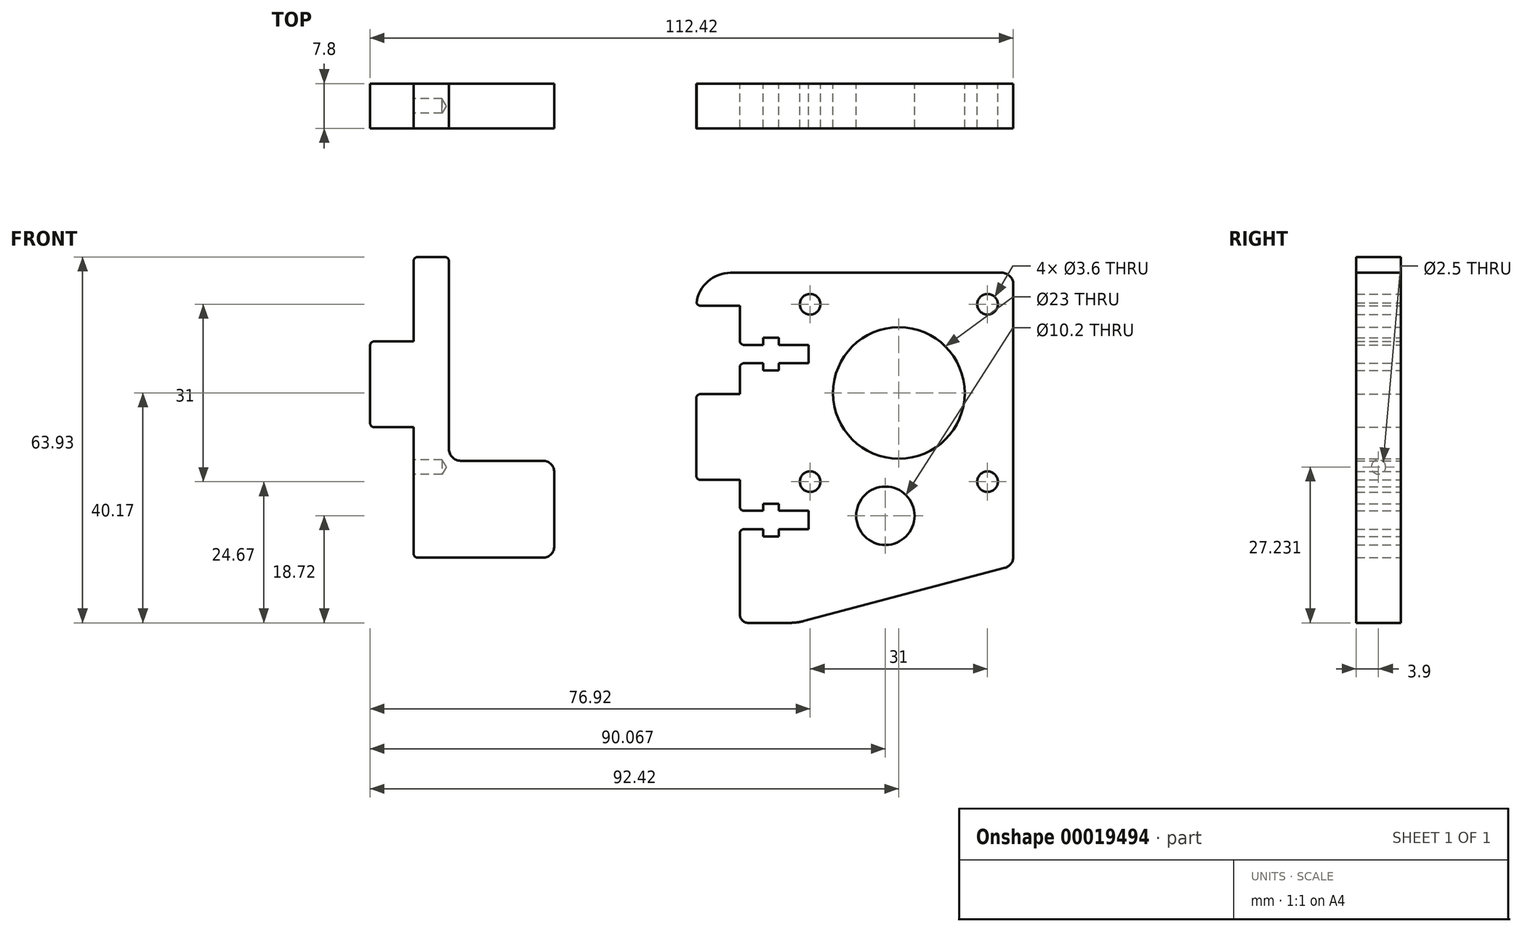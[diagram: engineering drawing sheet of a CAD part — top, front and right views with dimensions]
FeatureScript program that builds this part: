
annotation { "Feature Type Name" : "Feature", "Feature Type Description" : "" }
export const myFeature = defineFeature(function(context is Context, id is Id, definition is map)
    precondition{}
    {
        {
            var Q0;
            Q0=qCreatedBy(makeId("Front.planeOp"),FACE);
            var sketch = newSketch(context, id + "F0", { "sketchPlane" : qUnion([Q0])});
            skLineSegment(sketch, "E0.top", {"start": v(0.75, -5.75) * mm, "end": v(7.6, -5.75) * mm});
            skLineSegment(sketch, "E0.left", {"start": v(0, -5) * mm, "end": v(0, -6) * mm});
            skLineSegment(sketch, "E1", {"start": v(7.6, -21.2) * mm, "end": v(0.75, -21.2) * mm});
            skLineSegment(sketch, "E2", {"start": v(0, -21.95) * mm, "end": v(0, -35.45) * mm});
            skLineSegment(sketch, "E3", {"start": v(0.75, -36.2) * mm, "end": v(7.6, -36.2) * mm});
            skLineSegment(sketch, "E4", {"start": v(7.6, -36.2) * mm, "end": v(7.6, -40.85) * mm});
            skLineSegment(sketch, "E5", {"start": v(7.6, -21.2) * mm, "end": v(7.6, -16.55) * mm});
            skLineSegment(sketch, "E6", {"start": v(8.35, -15.8) * mm, "end": v(11.7, -15.8) * mm});
            skLineSegment(sketch, "E7", {"start": v(11.7, -15.8) * mm, "end": v(11.7, -17.05) * mm});
            skLineSegment(sketch, "E8", {"start": v(11.7, -17.05) * mm, "end": v(14.4, -17.05) * mm});
            skLineSegment(sketch, "E9", {"start": v(14.4, -17.05) * mm, "end": v(14.4, -15.8) * mm});
            skLineSegment(sketch, "E10", {"start": v(14.4, -15.8) * mm, "end": v(19.6, -15.8) * mm});
            skLineSegment(sketch, "E11", {"start": v(19.6, -15.8) * mm, "end": v(19.6, -12.6) * mm});
            skLineSegment(sketch, "E12", {"start": v(19.6, -12.6) * mm, "end": v(14.4, -12.6) * mm});
            skLineSegment(sketch, "E13", {"start": v(14.4, -12.6) * mm, "end": v(14.4, -11.35) * mm});
            skLineSegment(sketch, "E14", {"start": v(14.4, -11.35) * mm, "end": v(11.7, -11.35) * mm});
            skLineSegment(sketch, "E15", {"start": v(11.7, -11.35) * mm, "end": v(11.7, -12.6) * mm});
            skLineSegment(sketch, "E16", {"start": v(11.7, -12.6) * mm, "end": v(8.35, -12.6) * mm});
            skLineSegment(sketch, "E17", {"start": v(7.6, -11.85) * mm, "end": v(7.6, -5.75) * mm});
            skLineSegment(sketch, "E18", {"start": v(8.35, -41.6) * mm, "end": v(11.7, -41.6) * mm});
            skLineSegment(sketch, "E19", {"start": v(11.7, -41.6) * mm, "end": v(11.7, -40.35) * mm});
            skLineSegment(sketch, "E20", {"start": v(11.7, -40.35) * mm, "end": v(14.4, -40.35) * mm});
            skLineSegment(sketch, "E21", {"start": v(14.4, -40.35) * mm, "end": v(14.4, -41.6) * mm});
            skLineSegment(sketch, "E22", {"start": v(14.4, -41.6) * mm, "end": v(19.6, -41.6) * mm});
            skLineSegment(sketch, "E23", {"start": v(19.6, -41.6) * mm, "end": v(19.6, -44.8) * mm});
            skLineSegment(sketch, "E24", {"start": v(19.6, -44.8) * mm, "end": v(14.4, -44.8) * mm});
            skLineSegment(sketch, "E25", {"start": v(14.4, -44.8) * mm, "end": v(14.4, -46.05) * mm});
            skLineSegment(sketch, "E26", {"start": v(14.4, -46.05) * mm, "end": v(11.7, -46.05) * mm});
            skLineSegment(sketch, "E27", {"start": v(11.7, -46.05) * mm, "end": v(11.7, -44.8) * mm});
            skLineSegment(sketch, "E28", {"start": v(11.7, -44.8) * mm, "end": v(8.35, -44.8) * mm});
            skCircle(sketch, "E29", {"center": v(50.9, -5.5) * mm, "radius": 1.8 * mm});
            skCircle(sketch, "E30", {"center": v(50.9, -36.5) * mm, "radius": 1.8 * mm});
            skCircle(sketch, "E31.1.0.0", {"center": v(19.9, -5.5) * mm, "radius": 1.8 * mm});
            skCircle(sketch, "E31.1.0.1", {"center": v(19.9, -36.5) * mm, "radius": 1.8 * mm});
            skLineSegment(sketch, "E31.direction1", {"start": v(50.9, -5.5) * mm, "end": v(19.9, -5.5) * mm, "construction": true});
            skPoint(sketch, "E32.visualSharp", {"position": v(0, -5.75) * mm});
            skArc(sketch, "E32.filletArc", {"start": v(0, -5) * mm, "mid": v(0.22, -5.53) * mm, "end": v(0.75, -5.75) * mm});
            skPoint(sketch, "E33.visualSharp", {"position": v(0, -21.2) * mm});
            skArc(sketch, "E33.filletArc", {"start": v(0.75, -21.2) * mm, "mid": v(0.22, -21.42) * mm, "end": v(0, -21.95) * mm});
            skPoint(sketch, "E34.visualSharp", {"position": v(0, -36.2) * mm});
            skArc(sketch, "E34.filletArc", {"start": v(0, -35.45) * mm, "mid": v(0.22, -35.98) * mm, "end": v(0.75, -36.2) * mm});
            skLineSegment(sketch, "E35.trimOffspring", {"start": v(7.6, -45.55) * mm, "end": v(7.6, -59.67) * mm});
            skCircle(sketch, "E36", {"center": v(35.4, -21) * mm, "radius": 11.5 * mm});
            skCircle(sketch, "E37", {"center": v(33.05, -42.45) * mm, "radius": 5.1 * mm});
            skLineSegment(sketch, "E38", {"start": v(55.4, -2) * mm, "end": v(55.4, -49.63) * mm});
            skLineSegment(sketch, "E39", {"start": v(9.1, -61.17) * mm, "end": v(16.3, -61.17) * mm});
            skLineSegment(sketch, "E40", {"start": v(18.86, -60.84) * mm, "end": v(53.91, -51.56) * mm});
            skPoint(sketch, "E41.visualSharp", {"position": v(55.4, -51.17) * mm});
            skArc(sketch, "E41.filletArc", {"start": v(53.91, -51.56) * mm, "mid": v(54.98, -50.85) * mm, "end": v(55.4, -49.63) * mm});
            skPoint(sketch, "E42.visualSharp", {"position": v(7.6, -61.17) * mm});
            skArc(sketch, "E42.filletArc", {"start": v(7.6, -59.67) * mm, "mid": v(8.04, -60.73) * mm, "end": v(9.1, -61.17) * mm});
            skPoint(sketch, "E43.visualSharp", {"position": v(17.6, -61.17) * mm});
            skArc(sketch, "E43.filletArc", {"start": v(16.3, -61.17) * mm, "mid": v(17.59, -61.09) * mm, "end": v(18.86, -60.84) * mm});
            skPoint(sketch, "E44.visualSharp", {"position": v(7.6, -44.8) * mm});
            skArc(sketch, "E44.filletArc", {"start": v(8.35, -44.8) * mm, "mid": v(7.82, -45.02) * mm, "end": v(7.6, -45.55) * mm});
            skPoint(sketch, "E45.visualSharp", {"position": v(7.6, -41.6) * mm});
            skArc(sketch, "E45.filletArc", {"start": v(7.6, -40.85) * mm, "mid": v(7.82, -41.38) * mm, "end": v(8.35, -41.6) * mm});
            skPoint(sketch, "E46.visualSharp", {"position": v(7.6, -15.8) * mm});
            skArc(sketch, "E46.filletArc", {"start": v(8.35, -15.8) * mm, "mid": v(7.82, -16.02) * mm, "end": v(7.6, -16.55) * mm});
            skPoint(sketch, "E47.visualSharp", {"position": v(7.6, -12.6) * mm});
            skArc(sketch, "E47.filletArc", {"start": v(7.6, -11.85) * mm, "mid": v(7.82, -12.38) * mm, "end": v(8.35, -12.6) * mm});
            skLineSegment(sketch, "E48.trimOffspring", {"start": v(6, 0) * mm, "end": v(53.4, 0) * mm});
            skArc(sketch, "E49.filletArc", {"start": v(55.4, -2) * mm, "mid": v(54.81, -0.59) * mm, "end": v(53.4, 0) * mm});
            skPoint(sketch, "E50.orphan", {"position": v(0, 0) * mm});
            skArc(sketch, "E51.filletArc", {"start": v(6, 0) * mm, "mid": v(1.76, -1.76) * mm, "end": v(0, -6) * mm});
            skPoint(sketch, "E52", {"position": v(19.6, -43.2) * mm});
            skPoint(sketch, "E53", {"position": v(19.6, -14.2) * mm});
            skLineSegment(sketch, "E54", {"start": v(-49.42, -11.99) * mm, "end": v(-56.27, -11.99) * mm});
            skLineSegment(sketch, "E55", {"start": v(-57.02, -12.74) * mm, "end": v(-57.02, -26.24) * mm});
            skLineSegment(sketch, "E56", {"start": v(-56.27, -26.99) * mm, "end": v(-49.42, -26.99) * mm});
            skPoint(sketch, "E57.visualSharp", {"position": v(-57.02, -11.99) * mm});
            skArc(sketch, "E57.filletArc", {"start": v(-56.27, -11.99) * mm, "mid": v(-56.8, -12.2) * mm, "end": v(-57.02, -12.74) * mm});
            skPoint(sketch, "E58.visualSharp", {"position": v(-57.02, -26.99) * mm});
            skArc(sketch, "E58.filletArc", {"start": v(-57.02, -26.24) * mm, "mid": v(-56.8, -26.77) * mm, "end": v(-56.27, -26.99) * mm});
            skLineSegment(sketch, "E59", {"start": v(-49.42, -26.99) * mm, "end": v(-49.42, -33.94) * mm, "construction": true});
            skLineSegment(sketch, "E60", {"start": v(-49.42, -11.99) * mm, "end": v(-49.42, 2.01) * mm});
            skLineSegment(sketch, "E61", {"start": v(-48.67, 2.76) * mm, "end": v(-43.97, 2.76) * mm});
            skLineSegment(sketch, "E62", {"start": v(19.9, -36.5) * mm, "end": v(19.9, -42.1) * mm, "construction": true});
            skLineSegment(sketch, "E63", {"start": v(-49.42, -33.94) * mm, "end": v(-43.22, -33.94) * mm, "construction": true});
            skLineSegment(sketch, "E64", {"start": v(-43.22, -33.94) * mm, "end": v(-43.22, -32.84) * mm, "construction": true});
            skLineSegment(sketch, "E65", {"start": v(-43.22, 2.01) * mm, "end": v(-43.22, -30.84) * mm});
            skLineSegment(sketch, "E66", {"start": v(-41.22, -32.84) * mm, "end": v(-26.82, -32.84) * mm});
            skLineSegment(sketch, "E67", {"start": v(-49.42, -26.99) * mm, "end": v(-49.42, -49.04) * mm});
            skLineSegment(sketch, "E68", {"start": v(-24.82, -34.84) * mm, "end": v(-24.82, -47.79) * mm});
            skLineSegment(sketch, "E69", {"start": v(-26.82, -49.79) * mm, "end": v(-48.67, -49.79) * mm});
            skPoint(sketch, "E70.visualSharp", {"position": v(-43.22, -32.84) * mm});
            skArc(sketch, "E70.filletArc", {"start": v(-43.22, -30.84) * mm, "mid": v(-42.63, -32.25) * mm, "end": v(-41.22, -32.84) * mm});
            skPoint(sketch, "E71.visualSharp", {"position": v(-24.82, -32.84) * mm});
            skArc(sketch, "E71.filletArc", {"start": v(-24.82, -34.84) * mm, "mid": v(-25.4, -33.42) * mm, "end": v(-26.82, -32.84) * mm});
            skPoint(sketch, "E72.visualSharp", {"position": v(-24.82, -49.79) * mm});
            skArc(sketch, "E72.filletArc", {"start": v(-26.82, -49.79) * mm, "mid": v(-25.4, -49.2) * mm, "end": v(-24.82, -47.79) * mm});
            skPoint(sketch, "E73.visualSharp", {"position": v(-49.42, -49.79) * mm});
            skArc(sketch, "E73.filletArc", {"start": v(-49.42, -49.04) * mm, "mid": v(-49.2, -49.57) * mm, "end": v(-48.67, -49.79) * mm});
            skPoint(sketch, "E74.visualSharp", {"position": v(-49.42, 2.76) * mm});
            skArc(sketch, "E74.filletArc", {"start": v(-48.67, 2.76) * mm, "mid": v(-49.2, 2.54) * mm, "end": v(-49.42, 2.01) * mm});
            skPoint(sketch, "E75.visualSharp", {"position": v(-43.22, 2.76) * mm});
            skArc(sketch, "E75.filletArc", {"start": v(-43.22, 2.01) * mm, "mid": v(-43.44, 2.54) * mm, "end": v(-43.97, 2.76) * mm});
            skSolve(sketch);
        }
        {
            var Q0;
            Q0=makeQuery(id+"F0.imprint","IMPRINT",FACE,{"disambiguationData":[TD([[makeQuery(id+"F0.imprint","IMPRINT",EDGE,{"derivedFrom":sQuery(id+"F0.wireOp",EDGE,"f731473a-8967-4a35-8d6e-0af33edacdf4.bottom")}),-1.0]])]});
            var Q1;
            Q1=makeQuery(id+"F0.imprint","IMPRINT",FACE,{"disambiguationData":[TD([[makeQuery(id+"F0.imprint","IMPRINT",EDGE,{"derivedFrom":sQuery(id+"F0.wireOp",EDGE,"E0.top")}),1.0]])]});
            extrude(context, id + "F1", {"entities" : qUnion([Q0, Q1]), "depth" : 7.8 * mm});
        }
        {
            var Q0;
            Q0=makeQuery(id+"F0.imprint","IMPRINT",FACE,{"disambiguationData":[TD([[makeQuery(id+"F0.imprint","IMPRINT",EDGE,{"derivedFrom":sQuery(id+"F0.wireOp",EDGE,"E54")}),1.0]])]});
            extrude(context, id + "F2", {"entities" : qUnion([Q0]), "depth" : 7.8 * mm});
        }
        {
            var Q0;
            Q0=makeQuery(id+"F2.opExtrude","SWEPT_FACE",FACE,{"disambiguationData":[OSD([sQuery(id+"F0.wireOp",EDGE,"E67")])]});
            cPlane(context, id + "F3", {"entities" : qUnion([Q0]), "cplaneType" : CPlaneType.OFFSET, "offset" : 0 * mm, "width" : 150 * mm, "height" : 150 * mm});
        }
        {
            var Q0;
            Q0=qCreatedBy(id+"F3.planeOp",FACE);
            var sketch = newSketch(context, id + "F4", { "sketchPlane" : qUnion([Q0])});
            skLineSegment(sketch, "E76.0.0", {"start": v(0, -26.99) * mm, "end": v(0, -49.04) * mm});
            skLineSegment(sketch, "E76.0.1", {"start": v(0, -49.04) * mm, "end": v(7.8, -49.04) * mm});
            skLineSegment(sketch, "E76.0.2", {"start": v(7.8, -49.04) * mm, "end": v(7.8, -26.99) * mm});
            skLineSegment(sketch, "E76.0.3", {"start": v(7.8, -26.99) * mm, "end": v(0, -26.99) * mm});
            skLineSegment(sketch, "E77", {"start": v(0, -33.94) * mm, "end": v(3.9, -33.94) * mm, "construction": true});
            skCircle(sketch, "E78", {"center": v(3.9, -33.94) * mm, "radius": 1.25 * mm});
            skSolve(sketch);
        }
        {
            var Q0;
            Q0=sQuery(id+"F4.wireOp",VERTEX,"E78.center");
            var Q1;
            Q1=makeQuery(id+"F2.opExtrude","SWEPT_BODY",BODY,{"disambiguationData":[OSD([sQuery(id+"F0.wireOp",EDGE,"E54"),sQuery(id+"F0.wireOp",EDGE,"E55"),sQuery(id+"F0.wireOp",EDGE,"E56"),sQuery(id+"F0.wireOp",EDGE,"E57.filletArc"),sQuery(id+"F0.wireOp",EDGE,"E58.filletArc"),sQuery(id+"F0.wireOp",EDGE,"E60"),sQuery(id+"F0.wireOp",EDGE,"E61"),sQuery(id+"F0.wireOp",EDGE,"E65"),sQuery(id+"F0.wireOp",EDGE,"E66"),sQuery(id+"F0.wireOp",EDGE,"E67"),sQuery(id+"F0.wireOp",EDGE,"E68"),sQuery(id+"F0.wireOp",EDGE,"E69"),sQuery(id+"F0.wireOp",EDGE,"E70.filletArc"),sQuery(id+"F0.wireOp",EDGE,"E71.filletArc"),sQuery(id+"F0.wireOp",EDGE,"E72.filletArc"),sQuery(id+"F0.wireOp",EDGE,"E73.filletArc"),sQuery(id+"F0.wireOp",EDGE,"E74.filletArc"),sQuery(id+"F0.wireOp",EDGE,"E75.filletArc")])]});
            hole(context, id + "F5", {"style" : HoleStyle.SIMPLE, "endStyle" : HoleEndStyle.BLIND, "holeDiameter" : 2.5 * mm, "holeDepth" : 5 * mm, "locations" : qUnion([Q0]), "scope" : qUnion([Q1])});
        }
    });
